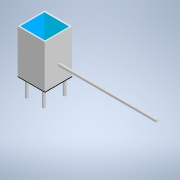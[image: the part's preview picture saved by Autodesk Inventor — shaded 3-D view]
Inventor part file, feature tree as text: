
AUTODESK INVENTOR PART (.ipt)
format: ipt  version: 2021 (Build 250183000, 183)  size: 136,192 bytes
history: native  units: mm
features: extrude x4, sketch x3
ambient origin geometry x8: Origin, YZ Plane, XZ Plane, XY Plane, X Axis, Y Axis, Z Axis, Center Point
bodies: Solid1 (feature_tree)
feature tree (7):
  sketch  "Sketch1"  dims[d0=50.0mm d1=50.0mm]
  extrude  "Extrusion1"  Depth=50.0mm
  extrude  "Extrusion2"  Depth=48.0mm TaperAngle=0.0deg
  extrude  "Extrusion3"  Depth=180.0mm
  extrude  "Extrusion6"  Depth=180.0mm
  sketch  "Sketch2"  dims[d2=80.0mm d3=0.0mm d4=48.0mm d5=0.0mm]
  sketch  "Sketch6"  dims[d6=5.0mm d9=5.0mm d10=5.0mm d11=5.0mm d12=30.0mm d13=0.0mm d20=25.992782mm d21=38.524198mm d22=5.0mm d23=180.0mm d24=0.0mm]
